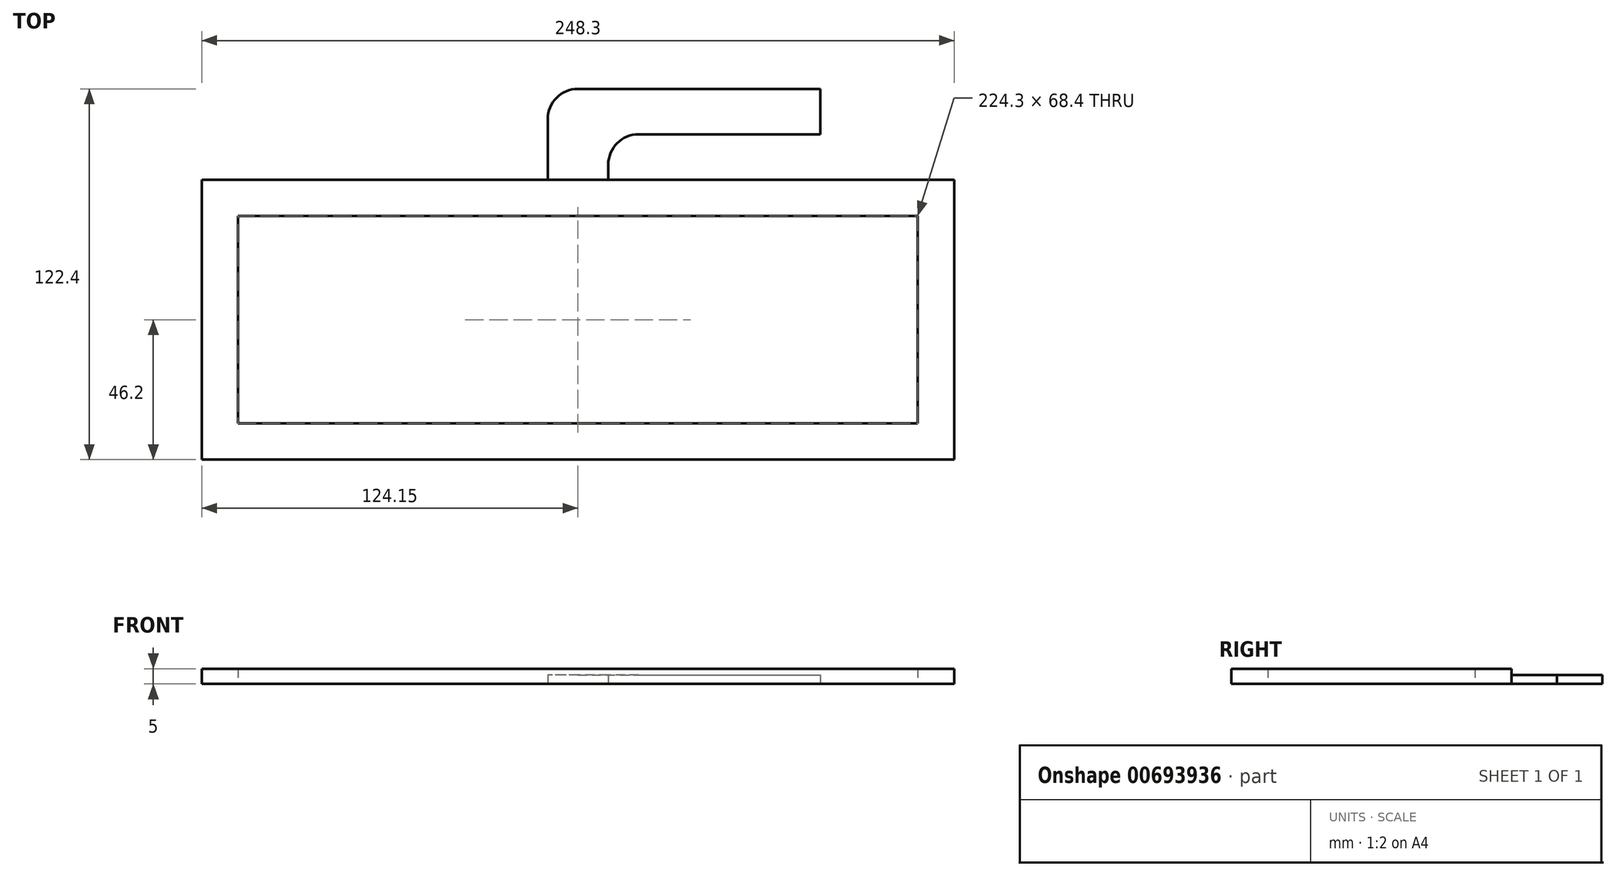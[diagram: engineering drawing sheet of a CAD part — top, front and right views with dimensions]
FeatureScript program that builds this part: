
annotation { "Feature Type Name" : "Feature", "Feature Type Description" : "" }
export const myFeature = defineFeature(function(context is Context, id is Id, definition is map)
    precondition{}
    {
        {
            var Q0;
            Q0=qCreatedBy(makeId("Top.planeOp"),FACE);
            var sketch = newSketch(context, id + "F0", { "sketchPlane" : qUnion([Q0])});
            skLineSegment(sketch, "E0.bottom", {"start": v(124.15, 46.2) * mm, "end": v(-124.15, 46.2) * mm});
            skLineSegment(sketch, "E0.top", {"start": v(124.15, -46.2) * mm, "end": v(-124.15, -46.2) * mm});
            skLineSegment(sketch, "E0.left", {"start": v(124.15, 46.2) * mm, "end": v(124.15, -46.2) * mm});
            skLineSegment(sketch, "E0.right", {"start": v(-124.15, 46.2) * mm, "end": v(-124.15, -46.2) * mm});
            skPoint(sketch, "E0.middle", {"position": v(0, 0) * mm});
            skLineSegment(sketch, "E1.0", {"start": v(112.15, 34.2) * mm, "end": v(-112.15, 34.2) * mm});
            skLineSegment(sketch, "E1.1", {"start": v(112.15, 34.2) * mm, "end": v(112.15, -34.2) * mm});
            skLineSegment(sketch, "E1.2", {"start": v(112.15, -34.2) * mm, "end": v(-112.15, -34.2) * mm});
            skLineSegment(sketch, "E1.3", {"start": v(-112.15, 34.2) * mm, "end": v(-112.15, -34.2) * mm});
            skLineSegment(sketch, "E2.bottom", {"start": v(-10, 46.2) * mm, "end": v(10, 46.2) * mm});
            skLineSegment(sketch, "E2.top", {"start": v(0, 76.2) * mm, "end": v(10, 76.2) * mm});
            skLineSegment(sketch, "E2.left", {"start": v(-10, 46.2) * mm, "end": v(-10, 66.2) * mm});
            skLineSegment(sketch, "E2.right", {"start": v(10, 46.2) * mm, "end": v(10, 51.2) * mm});
            skLineSegment(sketch, "E3.bottom", {"start": v(10, 76.2) * mm, "end": v(80, 76.2) * mm});
            skLineSegment(sketch, "E3.top", {"start": v(20, 61.2) * mm, "end": v(80, 61.2) * mm});
            skLineSegment(sketch, "E3.right", {"start": v(80, 76.2) * mm, "end": v(80, 61.2) * mm});
            skPoint(sketch, "E4.visualSharp", {"position": v(10, 61.2) * mm});
            skArc(sketch, "E4.filletArc", {"start": v(20, 61.2) * mm, "mid": v(12.93, 58.27) * mm, "end": v(10, 51.2) * mm});
            skPoint(sketch, "E5.visualSharp", {"position": v(-10, 76.2) * mm});
            skArc(sketch, "E5.filletArc", {"start": v(0, 76.2) * mm, "mid": v(-7.07, 73.27) * mm, "end": v(-10, 66.2) * mm});
            skSolve(sketch);
        }
        {
            var Q0;
            Q0=makeQuery(id+"F0.imprint","IMPRINT",FACE,{"disambiguationData":[TD([[makeQuery(id+"F0.imprint","IMPRINT",EDGE,{"derivedFrom":sQuery(id+"F0.wireOp",EDGE,"E0.top")}),-1.0]])]});
            extrude(context, id + "F1", {"entities" : qUnion([Q0]), "depth" : 5 * mm, "offsetDistance" : 25 * mm});
        }
        {
            var Q0;
            Q0=makeQuery(id+"F0.imprint","IMPRINT",FACE,{"disambiguationData":[TD([[makeQuery(id+"F0.imprint","IMPRINT",EDGE,{"derivedFrom":sQuery(id+"F0.wireOp",EDGE,"E2.top")}),-1.0]])]});
            extrude(context, id + "F2", {"entities" : qUnion([Q0]), "operationType" : NewBodyOperationType.ADD, "depth" : 3 * mm, "offsetDistance" : 25 * mm});
        }
    });
